# Revit family: SMALL UNDERWATER_LKPB0158CW.30
name_source: partatom
category: Luminarias
units: mm (PartAtom-declared; Revit-internal decimal feet)

## family parameters
Compartido = No
Corte con vacíos al cargar = No
Cota de conector redondo = Diámetro de uso
Origen de luz = Sí
Punto de cálculo de habitación = No
Se basa en plano de trabajo = Sí
Siempre vertical = No
Tipo de pieza = Normal

## types (1)
- SUB_LKPB0158CW.30
    Archivo de red fotométrica = SMALL UNDERWATER_LKPB0158CW 30°.IES
    Cambio de temperatura de color de luz atenuada = <Ninguno>
    Comentarios de vataje = 24V
    Descripción = LUMINARIA SUB ACUATICA TIPO PUNTUAL, ACABADO EN ACERO INOXIDABLE, CUPERO MOLDEADO EN CROMO, SELLO DE SILICON, VIDRIO TEMPLADO DE 7MM, 1 LED TIPO OSRAM CON UN CONSUMO TOTAL DE 2.6W, 174 LUMENES CON  UNA TEMPERATURA EN BLANCO CALIDO 6000K, IP 68, IK 06, SUMERGIBLE MAXIMO 2M, CABLE H07RN DE 3M, APERTURA A 30 GRADOS, ALIMENTADA A 24V. REQUIERE ACCESORIOS.
    Elevación por defecto = 0 mm  [stored 0 ft]
    Fabricante = BRILLANT
    Filtro de color = 16777215
    Lámpara = OSRAM
    Modelo = LKPB0158CW.30
    Watt per fixture = 2.6
    Ángulo de inclinación = 60.00°

note: [stored X ft] marks values corroborated as IEEE doubles in the binary element streams (Revit-internal decimal feet)

## geometry (parser evidence)
native form markers: Blend x2
no freeform markers — native parametric forms only
